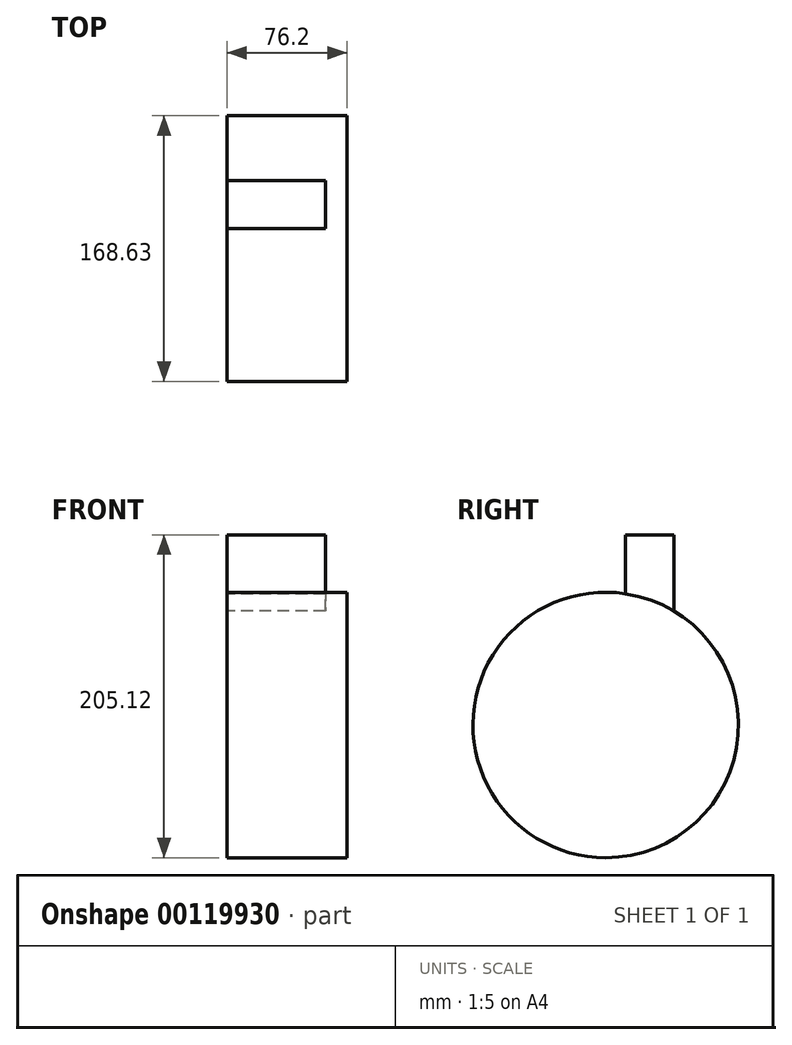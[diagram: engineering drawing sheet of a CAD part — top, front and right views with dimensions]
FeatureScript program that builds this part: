
annotation { "Feature Type Name" : "Feature", "Feature Type Description" : "" }
export const myFeature = defineFeature(function(context is Context, id is Id, definition is map)
    precondition{}
    {
        {
            var Q0;
            Q0=qCreatedBy(makeId("Top.planeOp"),FACE);
            var sketch = newSketch(context, id + "F0", { "sketchPlane" : qUnion([Q0])});
            skLineSegment(sketch, "E0.bottom", {"start": v(0, 0) * mm, "end": v(62.55, 0) * mm});
            skLineSegment(sketch, "E0.top", {"start": v(0, -30.62) * mm, "end": v(62.55, -30.62) * mm});
            skLineSegment(sketch, "E0.left", {"start": v(0, 0) * mm, "end": v(0, -30.62) * mm});
            skLineSegment(sketch, "E0.right", {"start": v(62.55, 0) * mm, "end": v(62.55, -30.62) * mm});
            skSolve(sketch);
        }
        {
            var Q0;
            Q0=makeQuery(id+"F0.imprint","IMPRINT",FACE,{"disambiguationData":[TD([[makeQuery(id+"F0.imprint","IMPRINT",EDGE,{"derivedFrom":sQuery(id+"F0.wireOp",EDGE,"E0.bottom")}),-1.0]])]});
            extrude(context, id + "F1", {"entities" : qUnion([Q0]), "depth" : 127 * mm});
        }
        {
            var Q0;
            Q0=qCreatedBy(makeId("Right.planeOp"),FACE);
            var sketch = newSketch(context, id + "F2", { "sketchPlane" : qUnion([Q0])});
            skCircle(sketch, "E1", {"center": v(-43.25, 6.2) * mm, "radius": 84.32 * mm});
            skSolve(sketch);
        }
        {
            var Q0;
            Q0=makeQuery(id+"F2.imprint","IMPRINT",FACE,{"disambiguationData":[TD([[makeQuery(id+"F2.imprint","IMPRINT",EDGE,{"derivedFrom":sQuery(id+"F2.wireOp",EDGE,"E1")}),1.0]])]});
            extrude(context, id + "F3", {"entities" : qUnion([Q0]), "operationType" : NewBodyOperationType.ADD, "depth" : 76.2 * mm});
        }
    });
